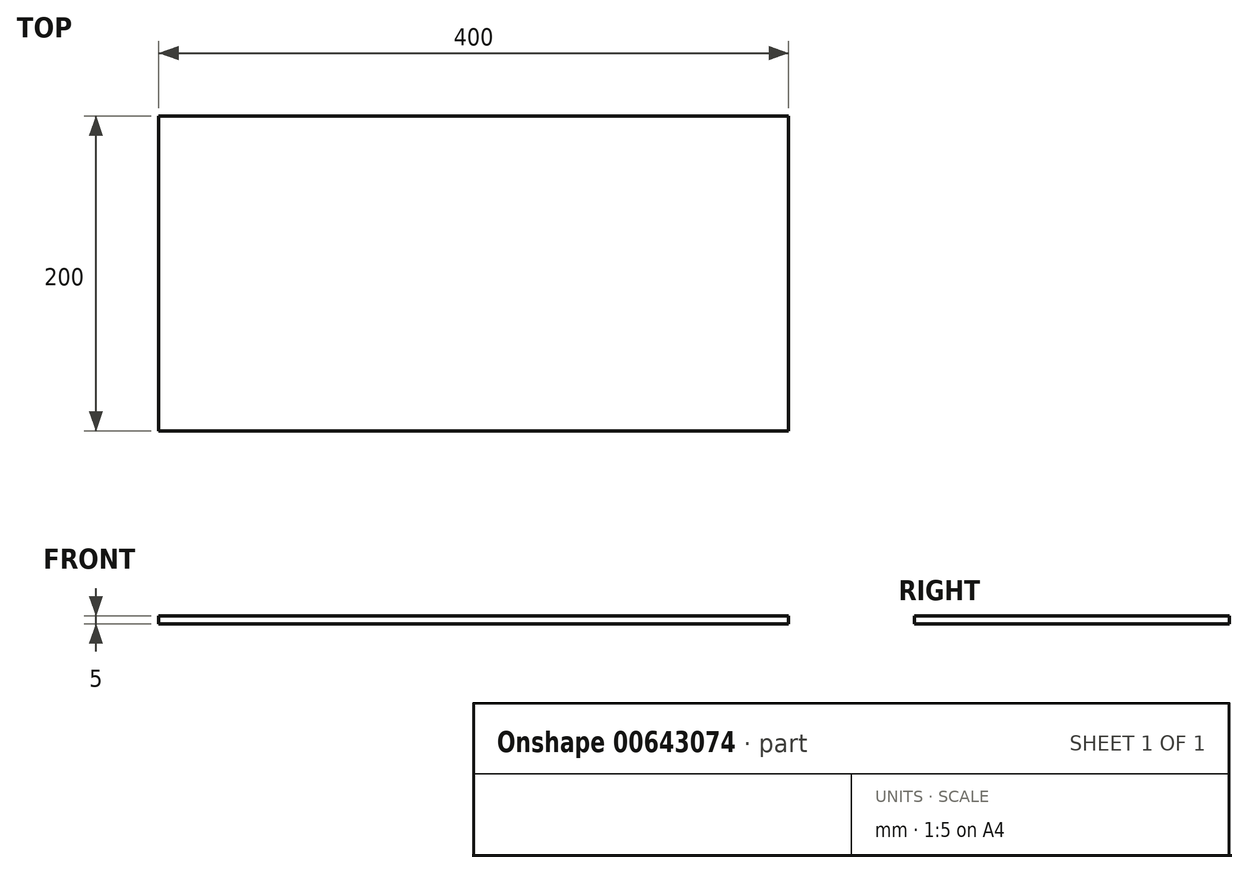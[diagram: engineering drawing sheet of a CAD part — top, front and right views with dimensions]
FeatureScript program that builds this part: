
annotation { "Feature Type Name" : "Feature", "Feature Type Description" : "" }
export const myFeature = defineFeature(function(context is Context, id is Id, definition is map)
    precondition{}
    {
        {
            var Q0;
            Q0=qCreatedBy(makeId("Top.planeOp"),FACE);
            var sketch = newSketch(context, id + "F0", { "sketchPlane" : qUnion([Q0])});
            skLineSegment(sketch, "E0.bottom", {"start": v(0, 0) * mm, "end": v(400, 0) * mm});
            skLineSegment(sketch, "E0.top", {"start": v(0, 200) * mm, "end": v(400, 200) * mm});
            skLineSegment(sketch, "E0.left", {"start": v(0, 0) * mm, "end": v(0, 200) * mm});
            skLineSegment(sketch, "E0.right", {"start": v(400, 0) * mm, "end": v(400, 200) * mm});
            skSolve(sketch);
        }
        {
            var Q0;
            Q0 = qSketchRegion(id + "F0", true);
            extrude(context, id + "F1", {"entities" : qUnion([Q0]), "depth" : 5 * mm, "offsetDistance" : 25 * mm});
        }
    });
